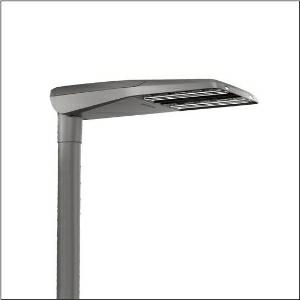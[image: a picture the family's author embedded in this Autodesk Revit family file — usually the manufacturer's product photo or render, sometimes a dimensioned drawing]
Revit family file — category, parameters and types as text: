
# Revit family: streetlight_sl_11_iq_midi___st0_5a_5xc3b51e08le_e4c9
name_source: partatom
category: Lighting Fixtures
units: mm (PartAtom-declared; Revit-internal decimal feet)

## family parameters
Cut with Voids When Loaded = No
Host = Face
Light Source = No
Part Type = Normal
Room Calculation Point = No
Round Connector Dimension = Use Diameter
Shared = No

## types (1)
- --- (1 x LED, 9120 lm, 60.4 W, 3000K)
    Apparent Load = 60 VA
    CIE Flux Codes = 43 74 97 100 100
    Color Rendering = 70
    Color Temperature = 3000K
    Default Elevation = 1800 mm
    Description = Streetlight SL 11 iQ midi, mast luminaire, primary light control with 3 zone facetted reflector, of plastic, silver coated, highly specular, primary optical cover: cover, of PMMA, transparent, light distribution: ST0.5a, light emission: direct distribution, primary light characteristic: asymmetric, installation type: post-top, side-entry, LED, High Power LED, rated luminous flux: 9.122lm, luminous efficacy: 151lm/W, light colour: 730, colour temperature: 3000K, control: optimised constant luminous flux control (CLO 2.0), Desk-Remote (wireless, voltage-free reading and setting of iQ features in the workshop via application-optimized NFC function/RFID function), Light-Fading, Smart-Wire, Night-Set, Lumen-Switch, Temp-Guard, Auto-Match, with cable H07RN-F 5x 1.5mm², mains connection: 220..240V, AC, 50/60Hz, connection cable pre-assembled, cable length: 8,5m, start of lifetime: 60W, end of lifetime: 63W, reduction: 31W, luminaire housing, of diecast aluminium, powder-coated, Siteco® metallic grey (DB 702S), length: 780mm, width: 376mm, height: 118mm, spigot size: 60/76mm (post-top) and 42/60/76mm (side-entry), mast flange for spigot size: 42mm: 5XC10008XM4, 60mm: 5XC10008XM2, 76/60mm: 5XC10108XM1, equipment: standard, protection rating (complete): IP66, insulation class (complete): insulation class II (safety insulation), certification: CE, ENEC, VDE, impact resistance: IK09, permissible operating ambient temperature for outdoor applications: -25..+50°C, standard-compliant lighting for roads and squares, packaging unit: 1 piece

Light Distribution: ST0.5a
    Height = 118 mm
    Lamp = 1 x LED
    Lamp Light Flux = 9120 lm
    Lamp Power = 60.4 W
    Lamp count = 1
    Length = 780 mm
    Luminous efficacy = 151 lm/W
    Manufacturer = Siteco
    ModVariant = No
    Model = 5XC3B51E08LE
    Number of Poles = 1
    OnlyDefault = Yes
    Power Factor = 1
    Product Name = Streetlight SL 11 iQ midi | ST0.5a
    Product group = mast luminaire | pylon top
    ProductGroupID = 6100
    Protection Class = Protection class II
    Protection Degree = IP 66
    RLX_Detail_Level = 1
    RlxData = <blob elided: 74725 chars, md5=620dde5f>
    Socket = socket
    Standby Power = 0 W
    System Light Flux = 9120 lm
    System Power = 60 W
    Type Comments = factory setting: luminous flux: 100 % | dim-lin: 254 | 520 mA
    Type Image = l_1005960.jpg
    URL = http://relux.com
    VarID = @adj_086859
    Voltage = 0 V
    Weight = 0.00 kg
    Width = 376 mm

## geometry (parser evidence)
native form markers: Blend x4, Sweep x10
no freeform markers — native parametric forms only
